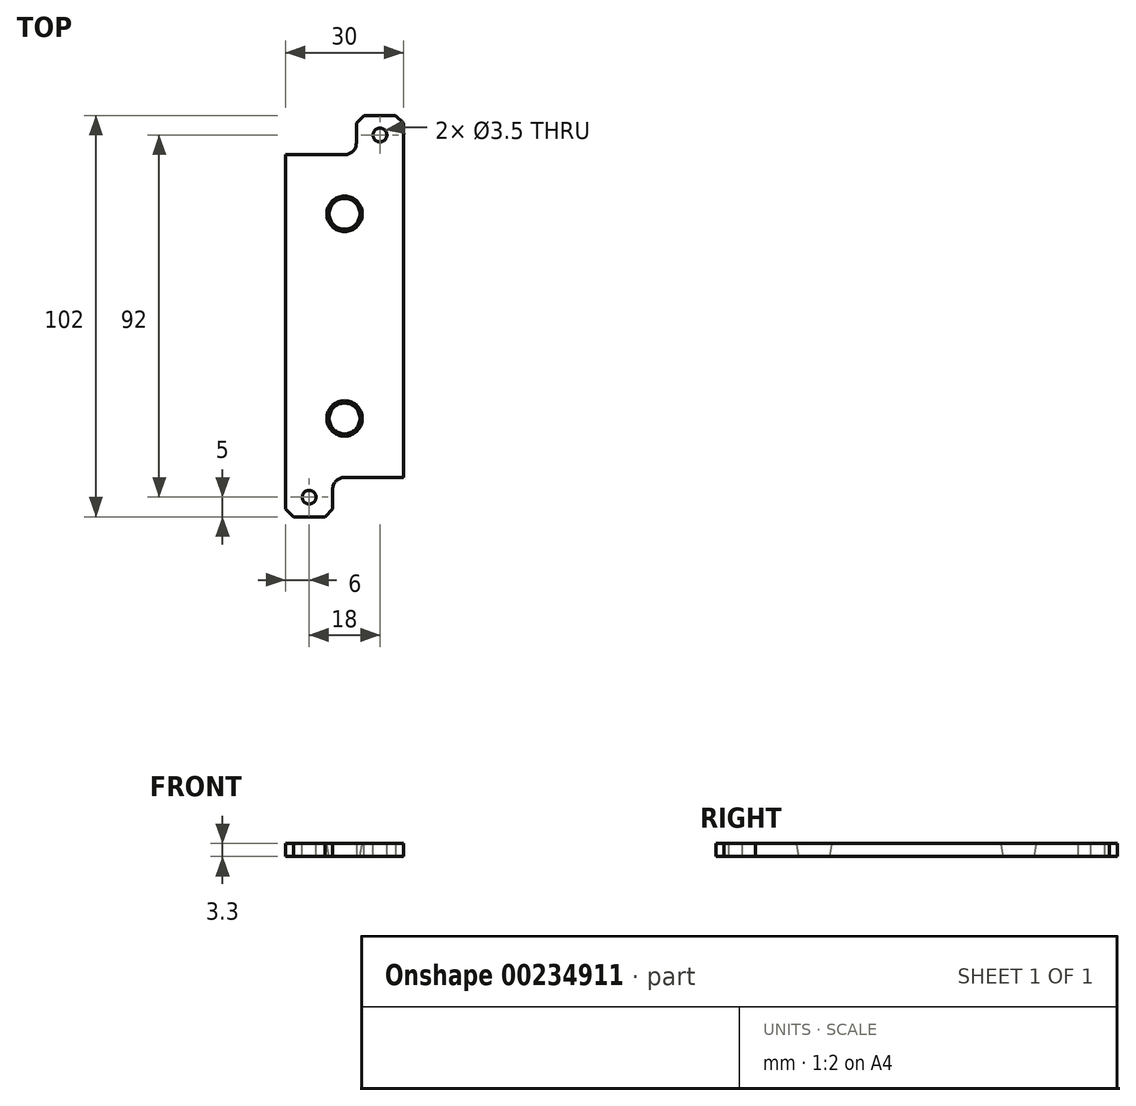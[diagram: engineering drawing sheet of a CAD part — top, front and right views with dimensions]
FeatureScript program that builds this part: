
annotation { "Feature Type Name" : "Feature", "Feature Type Description" : "" }
export const myFeature = defineFeature(function(context is Context, id is Id, definition is map)
    precondition{}
    {
        {
            var Q0;
            Q0=qCreatedBy(makeId("Top.planeOp"),FACE);
            var sketch = newSketch(context, id + "F0", { "sketchPlane" : qUnion([Q0])});
            skLineSegment(sketch, "E0.bottom", {"start": v(15, 41) * mm, "end": v(-15, 41) * mm});
            skLineSegment(sketch, "E0.top", {"start": v(15, -41) * mm, "end": v(-15, -41) * mm});
            skLineSegment(sketch, "E0.left", {"start": v(15, 41) * mm, "end": v(15, -41) * mm});
            skLineSegment(sketch, "E0.right", {"start": v(-15, 41) * mm, "end": v(-15, -41) * mm});
            skPoint(sketch, "E0.middle", {"position": v(0, 0) * mm});
            skLineSegment(sketch, "E1.bottom", {"start": v(15, 41) * mm, "end": v(3, 41) * mm});
            skLineSegment(sketch, "E1.top", {"start": v(15, 51) * mm, "end": v(3, 51) * mm});
            skLineSegment(sketch, "E1.left", {"start": v(15, 41) * mm, "end": v(15, 51) * mm});
            skLineSegment(sketch, "E1.right", {"start": v(3, 41) * mm, "end": v(3, 51) * mm});
            skLineSegment(sketch, "E2.bottom", {"start": v(-15, -41) * mm, "end": v(-3, -41) * mm});
            skLineSegment(sketch, "E2.top", {"start": v(-15, -51) * mm, "end": v(-3, -51) * mm});
            skLineSegment(sketch, "E2.left", {"start": v(-15, -41) * mm, "end": v(-15, -51) * mm});
            skLineSegment(sketch, "E2.right", {"start": v(-3, -41) * mm, "end": v(-3, -51) * mm});
            skSolve(sketch);
        }
        {
            var Q0;
            Q0 = qSketchRegion(id + "F0", true);
            extrude(context, id + "F1", {"entities" : qUnion([Q0]), "depth" : 3.3 * mm});
        }
        {
            var Q0;
            Q0=makeQuery(id+"F1.opExtrude","SWEPT_EDGE",EDGE,{"disambiguationData":[OSD([sQuery(id+"F0.wireOp",EDGE,"E1.top"),sQuery(id+"F0.wireOp",EDGE,"E1.left")])]});
            var Q1;
            Q1=makeQuery(id+"F1.opExtrude","SWEPT_EDGE",EDGE,{"disambiguationData":[OSD([sQuery(id+"F0.wireOp",EDGE,"E1.top"),sQuery(id+"F0.wireOp",EDGE,"E1.right")])]});
            var Q2;
            Q2=makeQuery(id+"F1.opExtrude","SWEPT_EDGE",EDGE,{"disambiguationData":[OSD([sQuery(id+"F0.wireOp",EDGE,"E2.top"),sQuery(id+"F0.wireOp",EDGE,"E2.left")])]});
            var Q3;
            Q3=makeQuery(id+"F1.opExtrude","SWEPT_EDGE",EDGE,{"disambiguationData":[OSD([sQuery(id+"F0.wireOp",EDGE,"E2.top"),sQuery(id+"F0.wireOp",EDGE,"E2.right")])]});
            chamfer(context, id + "F2", {"entities" : qUnion([Q0, Q1, Q2, Q3]), "width" : 2 * mm, "tangentPropagation" : true});
        }
        {
            var Q0;
            Q0=makeQuery(id+"F1.opExtrude","SWEPT_EDGE",EDGE,{"disambiguationData":[OSD([sQuery(id+"F0.wireOp",EDGE,"E0.bottom"),sQuery(id+"F0.wireOp",EDGE,"E1.bottom"),sQuery(id+"F0.wireOp",EDGE,"E1.right")])]});
            fillet(context, id + "F3", {"entities" : qUnion([Q0]), "radius" : 3 * mm, "tangentPropagation" : true, "allowEdgeOverflow" : false});
        }
        {
            var Q0;
            Q0=makeQuery(id+"F1.opExtrude","SWEPT_EDGE",EDGE,{"disambiguationData":[OSD([sQuery(id+"F0.wireOp",EDGE,"E0.top"),sQuery(id+"F0.wireOp",EDGE,"E2.bottom"),sQuery(id+"F0.wireOp",EDGE,"E2.right")])]});
            fillet(context, id + "F4", {"entities" : qUnion([Q0]), "radius" : 3 * mm, "tangentPropagation" : true, "allowEdgeOverflow" : false});
        }
        {
            var Q0;
            Q0=makeQuery(id+"F1.opExtrude","CAP_FACE",FACE,{"disambiguationData":[OSD([sQuery(id+"F0.wireOp",EDGE,"E0.bottom"),sQuery(id+"F0.wireOp",EDGE,"E0.top"),sQuery(id+"F0.wireOp",EDGE,"E0.left"),sQuery(id+"F0.wireOp",EDGE,"E0.right"),sQuery(id+"F0.wireOp",EDGE,"E1.top"),sQuery(id+"F0.wireOp",EDGE,"E1.left"),sQuery(id+"F0.wireOp",EDGE,"E1.right"),sQuery(id+"F0.wireOp",EDGE,"E2.top"),sQuery(id+"F0.wireOp",EDGE,"E2.left"),sQuery(id+"F0.wireOp",EDGE,"E2.right")])],"isStart":false});
            var sketch = newSketch(context, id + "F5", { "sketchPlane" : qUnion([Q0])});
            skLineSegment(sketch, "E3", {"start": v(9, 51) * mm, "end": v(9, 41) * mm, "construction": true});
            skCircle(sketch, "E4", {"center": v(9, 46) * mm, "radius": 1.75 * mm});
            skLineSegment(sketch, "E5", {"start": v(-9, -51) * mm, "end": v(-9, -41) * mm, "construction": true});
            skCircle(sketch, "E6", {"center": v(-9, -46) * mm, "radius": 1.75 * mm});
            skSolve(sketch);
        }
        {
            var Q0;
            Q0 = qSketchRegion(id + "F5", true);
            extrude(context, id + "F6", {"entities" : qUnion([Q0]), "operationType" : NewBodyOperationType.REMOVE, "oppositeDirection" : true, "depth" : 25 * mm});
        }
        {
            var Q0;
            Q0=makeQuery(id+"F1.opExtrude","CAP_FACE",FACE,{"disambiguationData":[OSD([sQuery(id+"F0.wireOp",EDGE,"E0.bottom"),sQuery(id+"F0.wireOp",EDGE,"E0.top"),sQuery(id+"F0.wireOp",EDGE,"E0.left"),sQuery(id+"F0.wireOp",EDGE,"E0.right"),sQuery(id+"F0.wireOp",EDGE,"E1.top"),sQuery(id+"F0.wireOp",EDGE,"E1.left"),sQuery(id+"F0.wireOp",EDGE,"E1.right"),sQuery(id+"F0.wireOp",EDGE,"E2.top"),sQuery(id+"F0.wireOp",EDGE,"E2.left"),sQuery(id+"F0.wireOp",EDGE,"E2.right")])],"isStart":false});
            var sketch = newSketch(context, id + "F7", { "sketchPlane" : qUnion([Q0])});
            skLineSegment(sketch, "E7", {"start": v(0, 41) * mm, "end": v(0, 0) * mm, "construction": true});
            skLineSegment(sketch, "E8", {"start": v(0, 0) * mm, "end": v(0, -41) * mm, "construction": true});
            skCircle(sketch, "E9", {"center": v(0, 26) * mm, "radius": 2.5 * mm});
            skCircle(sketch, "E10", {"center": v(0, -26) * mm, "radius": 2.5 * mm});
            skSolve(sketch);
        }
        {
            var Q0;
            Q0 = qSketchRegion(id + "F7", true);
            extrude(context, id + "F8", {"entities" : qUnion([Q0]), "operationType" : NewBodyOperationType.REMOVE, "oppositeDirection" : true, "depth" : 25 * mm});
        }
        {
            var Q0;
            Q0=makeQuery(id+"F1.opExtrude","CAP_FACE",FACE,{"disambiguationData":[OSD([sQuery(id+"F0.wireOp",EDGE,"E0.bottom"),sQuery(id+"F0.wireOp",EDGE,"E0.top"),sQuery(id+"F0.wireOp",EDGE,"E0.left"),sQuery(id+"F0.wireOp",EDGE,"E0.right"),sQuery(id+"F0.wireOp",EDGE,"E1.top"),sQuery(id+"F0.wireOp",EDGE,"E1.left"),sQuery(id+"F0.wireOp",EDGE,"E1.right"),sQuery(id+"F0.wireOp",EDGE,"E2.top"),sQuery(id+"F0.wireOp",EDGE,"E2.left"),sQuery(id+"F0.wireOp",EDGE,"E2.right")])],"isStart":false});
            var sketch = newSketch(context, id + "F9", { "sketchPlane" : qUnion([Q0])});
            skCircle(sketch, "E11", {"center": v(0, 26) * mm, "radius": 4.5 * mm});
            skCircle(sketch, "E12", {"center": v(0, -26) * mm, "radius": 4.5 * mm});
            skSolve(sketch);
        }
        {
            var Q0;
            Q0 = qSketchRegion(id + "F9", true);
            extrude(context, id + "F10", {"entities" : qUnion([Q0]), "operationType" : NewBodyOperationType.REMOVE, "oppositeDirection" : true, "depth" : 25 * mm, "hasDraft" : true, "draftAngle" : 10 * degree, "draftPullDirection" : true});
        }
    });
